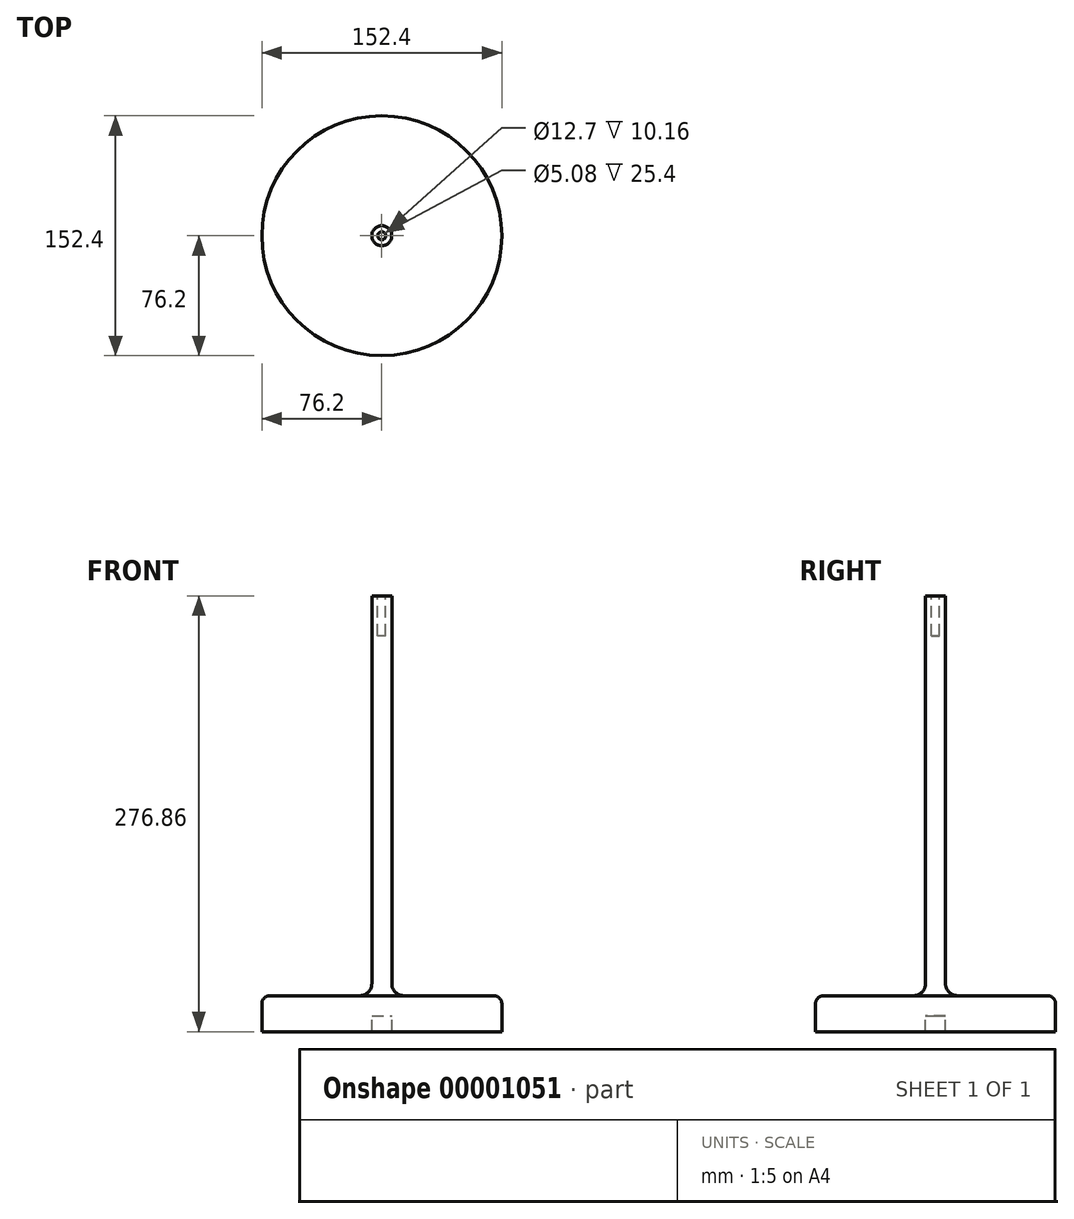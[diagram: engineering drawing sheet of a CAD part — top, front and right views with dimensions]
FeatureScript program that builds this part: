
annotation { "Feature Type Name" : "Feature", "Feature Type Description" : "" }
export const myFeature = defineFeature(function(context is Context, id is Id, definition is map)
    precondition{}
    {
        {
            var Q0;
            Q0=qCreatedBy(makeId("Top.planeOp"),FACE);
            var sketch = newSketch(context, id + "F0", { "sketchPlane" : qUnion([Q0])});
            skCircle(sketch, "E0", {"center": v(0, 0) * mm, "radius": 76.2 * mm});
            skSolve(sketch);
        }
        {
            var Q0;
            Q0=makeQuery(id+"F0.imprint","IMPRINT",FACE,{"disambiguationData":[TD([[makeQuery(id+"F0.imprint","IMPRINT",EDGE,{"derivedFrom":sQuery(id+"F0.wireOp",EDGE,"E0")}),1.0]])]});
            extrude(context, id + "F1", {"entities" : qUnion([Q0]), "depth" : 12.7 * mm});
        }
        {
            var Q0;
            Q0=makeQuery(id+"F1.opExtrude","CAP_EDGE",EDGE,{"disambiguationData":[OSD([sQuery(id+"F0.wireOp",EDGE,"E0")])],"isStart":false});
            fillet(context, id + "F2", {"entities" : qUnion([Q0]), "radius" : 5.08 * mm, "tangentPropagation" : true, "allowEdgeOverflow" : false});
        }
        {
            var Q0;
            Q0=makeQuery(id+"F1.opExtrude","CAP_FACE",FACE,{"disambiguationData":[OSD([sQuery(id+"F0.wireOp",EDGE,"E0")])],"isStart":false});
            var sketch = newSketch(context, id + "F3", { "sketchPlane" : qUnion([Q0])});
            skCircle(sketch, "E1", {"center": v(0, 0) * mm, "radius": 6.35 * mm});
            skSolve(sketch);
        }
        {
            var Q0;
            Q0=makeQuery(id+"F3.imprint","IMPRINT",FACE,{"disambiguationData":[TD([[makeQuery(id+"F3.imprint","IMPRINT",EDGE,{"derivedFrom":sQuery(id+"F3.wireOp",EDGE,"E1")}),1.0]])]});
            extrude(context, id + "F4", {"entities" : qUnion([Q0]), "operationType" : NewBodyOperationType.ADD, "depth" : 254 * mm});
        }
        {
            var Q0;
            Q0=makeQuery(id+"F1.opExtrude","CAP_FACE",FACE,{"disambiguationData":[OSD([sQuery(id+"F0.wireOp",EDGE,"E0")])],"isStart":false});
            fillet(context, id + "F5", {"entities" : qUnion([Q0]), "radius" : 7.62 * mm, "allowEdgeOverflow" : false});
        }
        {
            var Q0;
            Q0=makeQuery(id+"F1.opExtrude","CAP_FACE",FACE,{"disambiguationData":[OSD([sQuery(id+"F0.wireOp",EDGE,"E0")])],"isStart":true});
            var sketch = newSketch(context, id + "F6", { "sketchPlane" : qUnion([Q0])});
            skCircle(sketch, "E2", {"center": v(0, 0) * mm, "radius": 6.35 * mm});
            skSolve(sketch);
        }
        {
            var Q0;
            Q0=makeQuery(id+"F6.imprint","IMPRINT",FACE,{"disambiguationData":[TD([[makeQuery(id+"F6.imprint","IMPRINT",EDGE,{"derivedFrom":sQuery(id+"F6.wireOp",EDGE,"E2")}),-1.0]])]});
            extrude(context, id + "F7", {"entities" : qUnion([Q0]), "operationType" : NewBodyOperationType.ADD, "depth" : 10.16 * mm});
        }
        {
            var Q0;
            Q0=makeQuery(id+"F4.opExtrude","CAP_FACE",FACE,{"disambiguationData":[OSD([sQuery(id+"F3.wireOp",EDGE,"E1")])],"isStart":false});
            var sketch = newSketch(context, id + "F8", { "sketchPlane" : qUnion([Q0])});
            skCircle(sketch, "E3", {"center": v(0, 0) * mm, "radius": 2.54 * mm});
            skSolve(sketch);
        }
        {
            var Q0;
            Q0=makeQuery(id+"F8.imprint","IMPRINT",FACE,{"disambiguationData":[TD([[makeQuery(id+"F8.imprint","IMPRINT",EDGE,{"derivedFrom":sQuery(id+"F8.wireOp",EDGE,"E3")}),1.0]])]});
            extrude(context, id + "F9", {"entities" : qUnion([Q0]), "operationType" : NewBodyOperationType.REMOVE, "oppositeDirection" : true, "depth" : 25.4 * mm});
        }
    });
